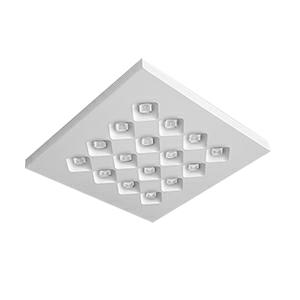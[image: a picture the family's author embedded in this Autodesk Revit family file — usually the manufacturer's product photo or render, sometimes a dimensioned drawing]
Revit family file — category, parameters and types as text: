
# Revit family: 3f_filippi_-_3f_diagon_3f_filippi_-_23002_a0686_-_3f_diagon_25w-830_596x596___corn_plaf__0c54
name_source: partatom
category: Lighting Fixtures
units: mm (PartAtom-declared; Revit-internal decimal feet)

## family parameters
Cut with Voids When Loaded = No
Host = Face
Light Source = No
Part Type = Normal
Room Calculation Point = No
Round Connector Dimension = Use Diameter
Shared = No

## types (1)
- 3F Filippi - 3F Dìagon (1 x LED, 4038 lm, 28 W, 3000 K)
    Apparent Load = 28 VA
    Approval mark = CE
    CIE Flux Codes = 67 96 100 100 100
    Color Rendering = 80
    Color Temperature = 3000 K
    Control Gear = Electronic ballast
    Default Elevation = 1800 mm
    Description = ILLUMINOTECHNICAL
Luminous efficiency 100% (DLOR 100%, ULOR 0%).
Initial luminous flux of the luminaire 4038 lm.
Direct symmetric distribution.
Installation Interdistance Transv.D = 1.39 x hu - Long.D = 1.39 x hu.
Average luminance <1500 cd/m² for radial angles >65°.
Tabular UGR (CIE 117 - 4H-8H; S=0.25H; 70/50/20): RUG 17.2 - 17.2.
Beam angle: 93° - 92°.
Luminous efficacy 144 lm/W.
Lifetime (L95/B10): 30000 h. (tq+25°C)
Lifetime (L90/B10): 50000 h. (tq+25°C)
Lifetime (L80/B10): 80000 h. (tq+25°C)
Lifetime (L75/B10): 100000 h. (tq+25°C)
Sudden decreased luminous flux after 50000 hours: 0% (C0).
Photobiological safety in compliance with IEC/TR 62778: RG0 risk exempt, (IEC 62471).
In compliance with IEC/EN 62722-2-1 - IEC/EN 62717 standards.

SOURCE
Squared LED module 25W/830.
Energy efficiency class (UE 2019/2020 - UE 2019/2015): C.
CIE 13.3 Colour rendering index: CRI >80 (R9 <50%).
IES TM-30 Fidelity Index: Rf = 84 Rg = 95.
CCT nominal colour temperature 3000 K.
Colour initial tolerance (MacAdam): SDCM 3.

MECHANICAL
Housing in hot-galvanised steel, painted in white polyester.
Honeycombed diagonal screen in white anti-glare polycarbonate.
Rhomboidal lenses with differentiated surfaces, etched and prismatic to optimise the orientation of the luminous flux, in transparent methacrylate (PMMA).
Luminaire with limited surface temperature. - D - (EN 60598-2-24)
Dimensions: 600x600 mm, height 40 mm. Weight 6.22 kg.
IP43 protection degree for exposed part, IP20 for recessed part.
Mechanical strength to impacts IK06 (1 joule).
Glow-wire test resistance 650°C.

ELECTRICAL
Halogen Free electronic wiring 230V-50/60Hz, power factor 0.95, THD <25%, constant output current, class I, 1 driver.
Power of the luminaire 28 W.
ENEC - CE.
SAFE FLICKER: PstLM=<1 and SVM=<0.4 (IEC TR 61547-1 and IEC TR 63158), to ensure a more comfortable and safe light.
Luminaire compliant with EN 60598-2-22 for power supply from a centralised emergency system CPSS (Central Power Supply System), not incorporated in the luminaire - high risk areas excluded. The default power and flux are 100% in AC and 100% in DC.
Ambient temperature from 0°C to +25°C.
Temperature class T6 max 85°C.
Quick connection.
Relative humidity UR: <85%.

INSTALLATION
Ceiling.
Height only 40 mm.
All accessories dedicated to this product are available on the Catalog and on our website www.3F-Filippi.com.

ACCESSORIES
A0686 - 596x596 Diagon frame for Ceiling installation.

APPLICATIONS
Environments: staterooms, with VDTs, offices.
Environments with exacting visual tasks, where diffused soft light for optimum visual comfort is required.

WARNING
Luminaire designed for disposal/recycling at end-of-life.
Replaceable (LED only) light source by a professional. Replaceable control gear by a professional.
    Height = 0 mm  [stored 0 ft]
    Lamp = 1 x LED
    Lamp Light Flux = 4038 lm
    Lamp Power = 28 W
    Lamp count = 1
    Length = 600 mm
    Lifetime = 50000 h
    Luminous efficacy = 144 lm/W
    Manufacturer = 3F Filippi
    ModVariant = No
    Model = 3F Filippi - 23002+A0686 - 3F Diagon 25W-830 596x596 + Corn.plaf.
    Mounting Place = Ceiling
    Mounting Type = Recessed
    Number of Poles = 1
    OnlyDefault = Yes
    Power Factor = 1
    Product Name = 3F Filippi - 3F Dìagon
    Product group = recessed luminaire
    ProductGroupID = 4
    Protection Class = Protection class I
    Protection Degree = IP 20
    RLX_Detail_Level = 1
    RLX_Emergency_Light_Flux = 0 lm
    RLX_Emergency_Type = 0
    RLX_Emergency_Type_DB = No
    RlxData = <blob elided: 96141 chars, md5=e3b7635a>
    Socket = socket
    Standby Power = 0 W
    System Light Flux = 4038 lm
    System Power = 28 W
    Type Comments = Product without accessories
    Type Image = 3ffilippi_3f_diagon__a0686.jpg
    URL = http://relux.com
    VarID = ---
    Voltage = 0 V
    Weight = 0.00 kg
    Width = 600 mm

note: [stored X ft] marks values corroborated as IEEE doubles in the binary element streams (Revit-internal decimal feet)

## geometry (parser evidence)
native form markers: Blend x4, Sweep x10
no freeform markers — native parametric forms only
